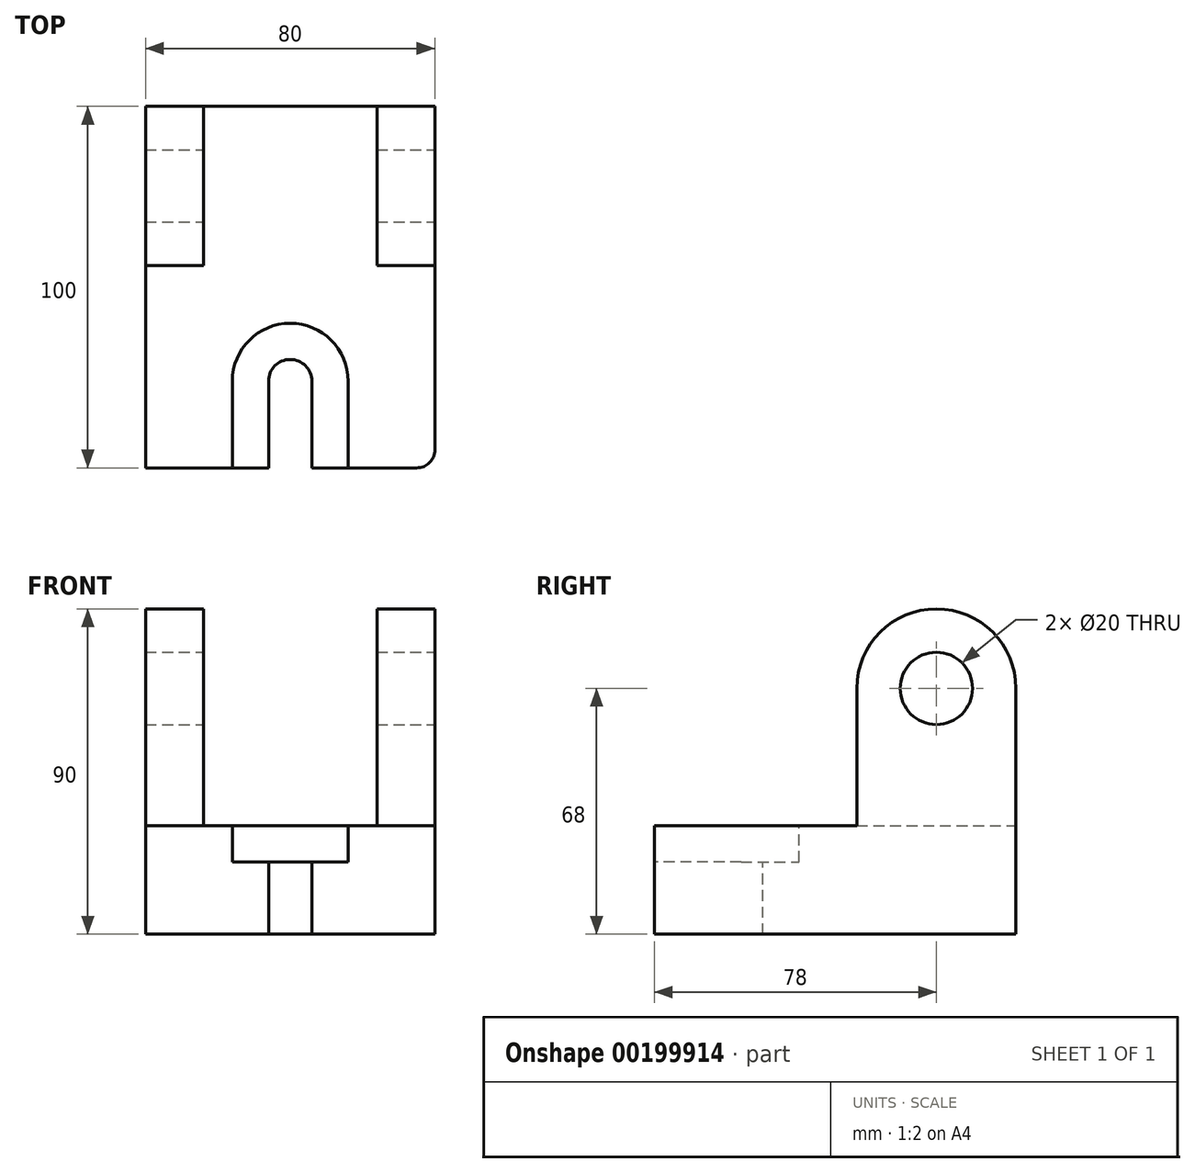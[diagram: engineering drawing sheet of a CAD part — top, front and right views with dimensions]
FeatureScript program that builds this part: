
annotation { "Feature Type Name" : "Feature", "Feature Type Description" : "" }
export const myFeature = defineFeature(function(context is Context, id is Id, definition is map)
    precondition{}
    {
        {
            var Q0;
            Q0=qCreatedBy(makeId("Front.planeOp"),FACE);
            var sketch = newSketch(context, id + "F0", { "sketchPlane" : qUnion([Q0])});
            skLineSegment(sketch, "E0", {"start": v(0, 0) * mm, "end": v(80, 0) * mm});
            skLineSegment(sketch, "E1", {"start": v(80, 0) * mm, "end": v(80, 90) * mm});
            skLineSegment(sketch, "E2", {"start": v(80, 90) * mm, "end": v(64, 90) * mm});
            skLineSegment(sketch, "E3", {"start": v(0, 90) * mm, "end": v(0, 0) * mm});
            skLineSegment(sketch, "E4", {"start": v(0, 0) * mm, "end": v(0, 30) * mm});
            skLineSegment(sketch, "E5", {"start": v(0, 30) * mm, "end": v(0, 0) * mm});
            skLineSegment(sketch, "E6", {"start": v(0, 30) * mm, "end": v(80, 30) * mm});
            skLineSegment(sketch, "E7", {"start": v(16, 90) * mm, "end": v(0, 90) * mm});
            skLineSegment(sketch, "E8", {"start": v(16, 90) * mm, "end": v(16, 30) * mm});
            skLineSegment(sketch, "E9", {"start": v(64, 90) * mm, "end": v(64, 30) * mm});
            skSolve(sketch);
        }
        {
            var Q0;
            {var subQ4=sQuery(id+"F0.wireOp",EDGE,"E0");Q0=makeQuery(id+"F0.imprint","IMPRINT",FACE,{"disambiguationData":[TD([[makeQuery(id+"F0.imprint","IMPRINT",EDGE,{"derivedFrom":subQ4}),1.0]])]});}
            extrude(context, id + "F1", {"entities" : qUnion([Q0]), "depth" : 100 * mm});
        }
        {
            var Q0;
            {var subQ0=sQuery(id+"F0.wireOp",EDGE,"E3");Q0=makeQuery(id+"F0.imprint","IMPRINT",FACE,{"disambiguationData":[TD([[makeQuery(id+"F0.imprint","IMPRINT",EDGE,{"derivedFrom":subQ0}),1.0]])]});}
            var Q1;
            {var subQ0=sQuery(id+"F0.wireOp",EDGE,"E2");Q1=makeQuery(id+"F0.imprint","IMPRINT",FACE,{"disambiguationData":[TD([[makeQuery(id+"F0.imprint","IMPRINT",EDGE,{"derivedFrom":subQ0}),1.0]])]});}
            extrude(context, id + "F2", {"entities" : qUnion([Q0, Q1]), "operationType" : NewBodyOperationType.ADD, "depth" : 44 * mm});
        }
        {
            var Q0;
            Q0=makeQuery(id+"F1.opExtrude","CAP_EDGE",EDGE,{"disambiguationData":[OSD([sQuery(id+"F0.wireOp",EDGE,"E1")])],"isStart":false});
            var Q1;
            Q1=makeQuery(id+"F1.opExtrude","CAP_EDGE",EDGE,{"disambiguationData":[OSD([sQuery(id+"F0.wireOp",EDGE,"E5")])],"isStart":false});
            fillet(context, id + "F3", {"entities" : qUnion([Q0, Q1]), "radius" : 5 * mm, "tangentPropagation" : true, "allowEdgeOverflow" : false});
        }
        {
            var Q0;
            Q0=makeQuery(id+"F2.opExtrude","CAP_EDGE",EDGE,{"disambiguationData":[OSD([sQuery(id+"F0.wireOp",EDGE,"E2")])],"isStart":false});
            var Q1;
            Q1=makeQuery(id+"F2.opExtrude","CAP_EDGE",EDGE,{"disambiguationData":[OSD([sQuery(id+"F0.wireOp",EDGE,"E2")])],"isStart":true});
            var Q2;
            Q2=makeQuery(id+"F2.opExtrude","CAP_EDGE",EDGE,{"disambiguationData":[OSD([sQuery(id+"F0.wireOp",EDGE,"E7")])],"isStart":true});
            var Q3;
            Q3=makeQuery(id+"F2.opExtrude","CAP_EDGE",EDGE,{"disambiguationData":[OSD([sQuery(id+"F0.wireOp",EDGE,"E7")])],"isStart":false});
            fillet(context, id + "F4", {"entities" : qUnion([Q0, Q1, Q2, Q3]), "radius" : 22 * mm, "tangentPropagation" : true, "allowEdgeOverflow" : false});
        }
        {
            var Q0;
            {var subQ0=sQuery(id+"F0.wireOp",EDGE,"E1");Q0=makeQuery(id+"F2.boolean.opBoolean","MERGE",FACE,{"derivedFrom":[makeQuery(id+"F1.opExtrude","SWEPT_FACE",FACE,{"disambiguationData":[OSD([subQ0])]}),makeQuery(id+"F2.opExtrude","SWEPT_FACE",FACE,{"disambiguationData":[OSD([subQ0])]})]});}
            var sketch = newSketch(context, id + "F5", { "sketchPlane" : qUnion([Q0])});
            skLineSegment(sketch, "E10", {"start": v(-44, 68) * mm, "end": v(0, 68) * mm});
            skLineSegment(sketch, "E11", {"start": v(-22, 90) * mm, "end": v(-22, 68) * mm});
            skCircle(sketch, "E12", {"center": v(-22, 68) * mm, "radius": 10 * mm});
            skSolve(sketch);
        }
        {
            var Q0;
            {var subQ0=sQuery(id+"F5.wireOp",EDGE,"E11");var subQ1=sQuery(id+"F5.wireOp",EDGE,"E10");var subQ2=makeQuery(id+"F5.imprint","INTERSECT",VERTEX,{"derivedFrom":[subQ1,subQ0]});Q0=makeQuery(id+"F5.imprint","IMPRINT",FACE,{"disambiguationData":[TD([[makeQuery(id+"F5.imprint","IMPRINT",EDGE,{"disambiguationData":[TD([[subQ2,1.0]])],"derivedFrom":subQ1}),1.0]])]});}
            var Q1;
            {var subQ0=sQuery(id+"F5.wireOp",EDGE,"E11");var subQ1=sQuery(id+"F5.wireOp",EDGE,"E10");var subQ2=makeQuery(id+"F5.imprint","INTERSECT",VERTEX,{"derivedFrom":[subQ1,subQ0]});Q1=makeQuery(id+"F5.imprint","IMPRINT",FACE,{"disambiguationData":[TD([[makeQuery(id+"F5.imprint","IMPRINT",EDGE,{"disambiguationData":[TD([[subQ2,-1.0]])],"derivedFrom":subQ1}),1.0]])]});}
            var Q2;
            {var subQ0=sQuery(id+"F5.wireOp",EDGE,"E10");var subQ1=makeQuery(id+"F5.imprint","INTERSECT",VERTEX,{"derivedFrom":[subQ0,sQuery(id+"F5.wireOp",EDGE,"E11")]});Q2=makeQuery(id+"F5.imprint","IMPRINT",FACE,{"disambiguationData":[TD([[makeQuery(id+"F5.imprint","IMPRINT",EDGE,{"disambiguationData":[TD([[subQ1,1.0]])],"derivedFrom":subQ0}),-1.0]])]});}
            extrude(context, id + "F6", {"entities" : qUnion([Q0, Q1, Q2]), "operationType" : NewBodyOperationType.REMOVE, "oppositeDirection" : true, "depth" : 80 * mm});
        }
        {
            var Q0;
            Q0=makeQuery(id+"F1.opExtrude","SWEPT_FACE",FACE,{"disambiguationData":[OSD([sQuery(id+"F0.wireOp",EDGE,"E6")])]});
            var sketch = newSketch(context, id + "F7", { "sketchPlane" : qUnion([Q0])});
            skLineSegment(sketch, "E13", {"start": v(40, -100) * mm, "end": v(40, -76) * mm});
            skCircle(sketch, "E14", {"center": v(40, -76) * mm, "radius": 5.99 * mm});
            skLineSegment(sketch, "E15", {"start": v(45.99, -76) * mm, "end": v(45.99, -100) * mm});
            skLineSegment(sketch, "E16", {"start": v(34.01, -76) * mm, "end": v(34.01, -100) * mm});
            skLineSegment(sketch, "E17", {"start": v(34.01, -100) * mm, "end": v(45.99, -100) * mm});
            skCircle(sketch, "E18", {"center": v(40, -76) * mm, "radius": 16 * mm});
            skLineSegment(sketch, "E19", {"start": v(56, -76) * mm, "end": v(56, -100) * mm});
            skLineSegment(sketch, "E20", {"start": v(24, -76) * mm, "end": v(24, -100) * mm});
            skLineSegment(sketch, "E21", {"start": v(24, -100) * mm, "end": v(56, -100) * mm});
            skSolve(sketch);
        }
        {
            var Q0;
            {var subQ0=sQuery(id+"F7.wireOp",EDGE,"E21");var subQ1=sQuery(id+"F7.wireOp",EDGE,"E13");var subQ2=makeQuery(id+"F7.imprint","INTERSECT",VERTEX,{"derivedFrom":[subQ1,subQ0]});Q0=makeQuery(id+"F7.imprint","IMPRINT",FACE,{"disambiguationData":[TD([[makeQuery(id+"F7.imprint","IMPRINT",EDGE,{"disambiguationData":[TD([[subQ2,-1.0]])],"derivedFrom":subQ1}),-1.0]])]});}
            var Q1;
            {var subQ0=sQuery(id+"F7.wireOp",EDGE,"E21");var subQ1=sQuery(id+"F7.wireOp",EDGE,"E13");var subQ2=makeQuery(id+"F7.imprint","INTERSECT",VERTEX,{"derivedFrom":[subQ1,subQ0]});Q1=makeQuery(id+"F7.imprint","IMPRINT",FACE,{"disambiguationData":[TD([[makeQuery(id+"F7.imprint","IMPRINT",EDGE,{"disambiguationData":[TD([[subQ2,-1.0]])],"derivedFrom":subQ1}),1.0]])]});}
            var Q2;
            {var subQ0=sQuery(id+"F7.wireOp",EDGE,"E14");var subQ1=sQuery(id+"F7.wireOp",EDGE,"E13");var subQ2=makeQuery(id+"F7.imprint","INTERSECT",VERTEX,{"derivedFrom":[subQ1,subQ0]});Q2=makeQuery(id+"F7.imprint","IMPRINT",FACE,{"disambiguationData":[TD([[makeQuery(id+"F7.imprint","IMPRINT",EDGE,{"disambiguationData":[TD([[subQ2,1.0]])],"derivedFrom":subQ1}),-1.0]])]});}
            var Q3;
            {var subQ0=sQuery(id+"F7.wireOp",EDGE,"E14");var subQ1=sQuery(id+"F7.wireOp",EDGE,"E13");var subQ2=makeQuery(id+"F7.imprint","INTERSECT",VERTEX,{"derivedFrom":[subQ1,subQ0]});Q3=makeQuery(id+"F7.imprint","IMPRINT",FACE,{"disambiguationData":[TD([[makeQuery(id+"F7.imprint","IMPRINT",EDGE,{"disambiguationData":[TD([[subQ2,1.0]])],"derivedFrom":subQ1}),1.0]])]});}
            var Q4;
            {var subQ0=sQuery(id+"F7.wireOp",EDGE,"E14");var subQ1=makeQuery(id+"F7.imprint","INTERSECT",VERTEX,{"derivedFrom":[subQ0,sQuery(id+"F7.wireOp",EDGE,"E15")]});Q4=makeQuery(id+"F7.imprint","IMPRINT",FACE,{"disambiguationData":[TD([[makeQuery(id+"F7.imprint","IMPRINT",EDGE,{"disambiguationData":[TD([[subQ1,-1.0]])],"derivedFrom":subQ0}),1.0]])]});}
            extrude(context, id + "F8", {"entities" : qUnion([Q0, Q1, Q2, Q3, Q4]), "operationType" : NewBodyOperationType.REMOVE, "oppositeDirection" : true, "depth" : 30 * mm});
        }
        {
            var Q0;
            {var subQ1=sQuery(id+"F7.wireOp",EDGE,"E14");var subQ5=sQuery(id+"F7.wireOp",EDGE,"E15");var subQ6=makeQuery(id+"F7.imprint","INTERSECT",VERTEX,{"derivedFrom":[subQ1,subQ5]});Q0=makeQuery(id+"F7.imprint","IMPRINT",FACE,{"disambiguationData":[TD([[makeQuery(id+"F7.imprint","IMPRINT",EDGE,{"disambiguationData":[TD([[subQ6,-1.0]])],"derivedFrom":subQ1}),-1.0]])]});}
            var Q1;
            {var subQ5=sQuery(id+"F7.wireOp",EDGE,"E20");Q1=makeQuery(id+"F7.imprint","IMPRINT",FACE,{"disambiguationData":[TD([[makeQuery(id+"F7.imprint","IMPRINT",EDGE,{"derivedFrom":subQ5}),1.0]])]});}
            var Q2;
            {var subQ5=sQuery(id+"F7.wireOp",EDGE,"E19");Q2=makeQuery(id+"F7.imprint","IMPRINT",FACE,{"disambiguationData":[TD([[makeQuery(id+"F7.imprint","IMPRINT",EDGE,{"derivedFrom":subQ5}),-1.0]])]});}
            extrude(context, id + "F9", {"entities" : qUnion([Q0, Q1, Q2]), "operationType" : NewBodyOperationType.REMOVE, "oppositeDirection" : true, "depth" : 10 * mm});
        }
    });
